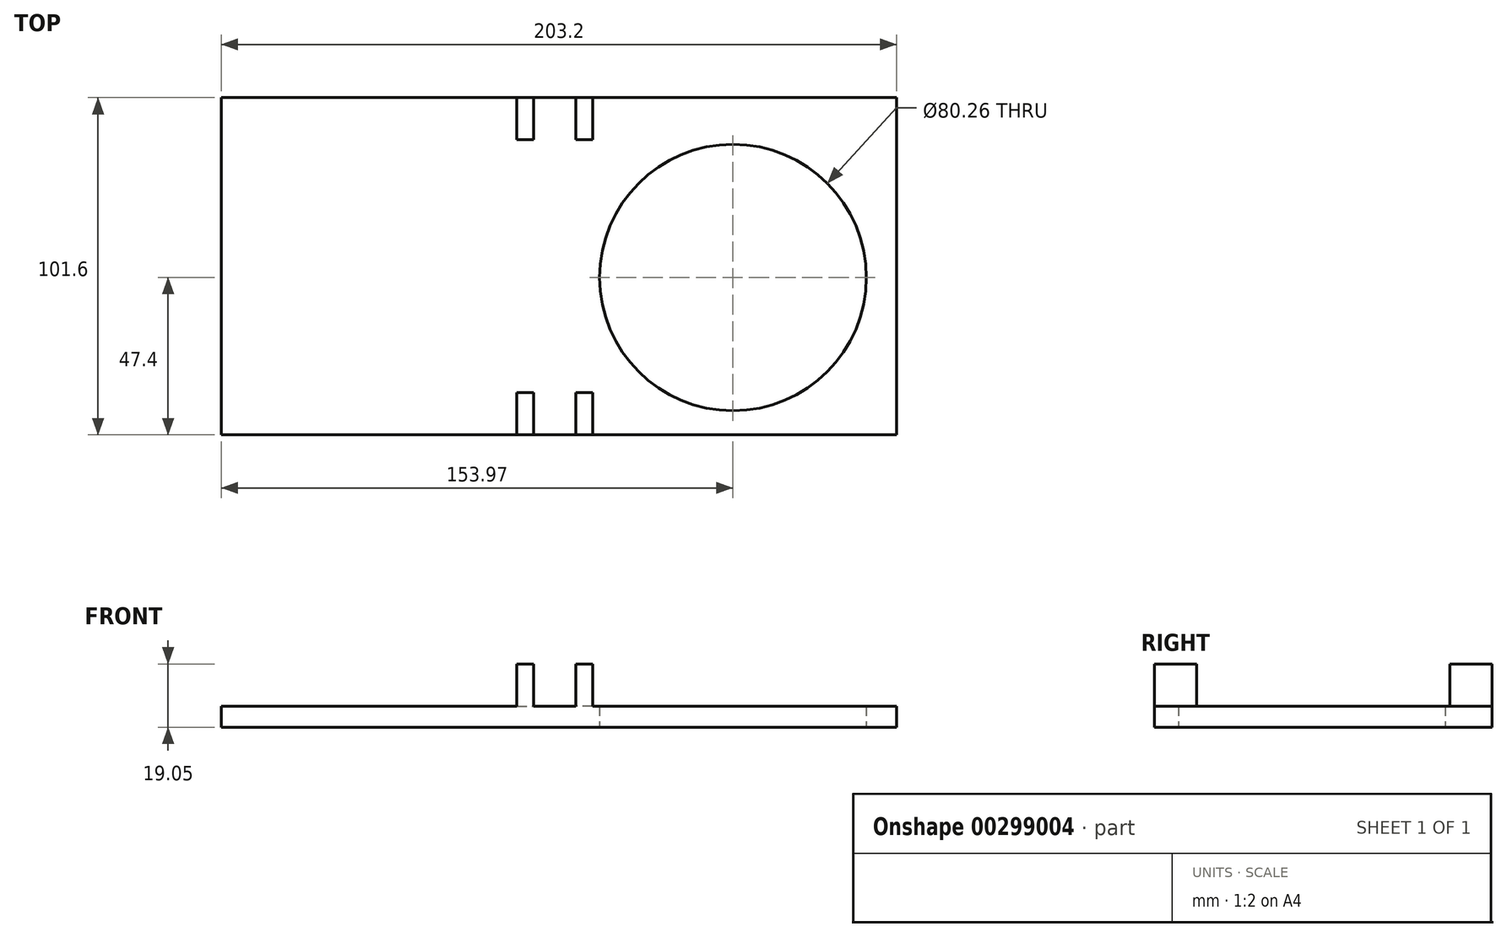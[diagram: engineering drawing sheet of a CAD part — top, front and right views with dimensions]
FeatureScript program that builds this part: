
annotation { "Feature Type Name" : "Feature", "Feature Type Description" : "" }
export const myFeature = defineFeature(function(context is Context, id is Id, definition is map)
    precondition{}
    {
        {
            var Q0;
            Q0=qCreatedBy(makeId("Top.planeOp"),FACE);
            var sketch = newSketch(context, id + "F0", { "sketchPlane" : qUnion([Q0])});
            skLineSegment(sketch, "E0.bottom", {"start": v(-77.88, 18.2) * mm, "end": v(125.32, 18.2) * mm});
            skLineSegment(sketch, "E0.top", {"start": v(-77.88, -83.4) * mm, "end": v(125.32, -83.4) * mm});
            skLineSegment(sketch, "E0.left", {"start": v(-77.88, 18.2) * mm, "end": v(-77.88, -83.4) * mm});
            skLineSegment(sketch, "E0.right", {"start": v(125.32, 18.2) * mm, "end": v(125.32, -83.4) * mm});
            skCircle(sketch, "E1", {"center": v(76.1, -36) * mm, "radius": 40.13 * mm});
            skSolve(sketch);
        }
        {
            var Q0;
            Q0 = qSketchRegion(id + "F0", true);
            extrude(context, id + "F1", {"entities" : qUnion([Q0]), "depth" : 6.35 * mm});
        }
        {
            var Q0;
            Q0=makeQuery(id+"F1.opExtrude","CAP_FACE",FACE,{"disambiguationData":[OSD([sQuery(id+"F0.wireOp",EDGE,"E0.bottom"),sQuery(id+"F0.wireOp",EDGE,"E0.top"),sQuery(id+"F0.wireOp",EDGE,"E0.left"),sQuery(id+"F0.wireOp",EDGE,"E0.right"),sQuery(id+"F0.wireOp",EDGE,"E1")])],"isStart":false});
            var sketch = newSketch(context, id + "F2", { "sketchPlane" : qUnion([Q0])});
            skLineSegment(sketch, "E2.bottom", {"start": v(33.88, -83.4) * mm, "end": v(28.8, -83.4) * mm});
            skLineSegment(sketch, "E2.top", {"start": v(33.88, -70.7) * mm, "end": v(28.8, -70.7) * mm});
            skLineSegment(sketch, "E2.left", {"start": v(33.88, -83.4) * mm, "end": v(33.88, -70.7) * mm});
            skLineSegment(sketch, "E2.right", {"start": v(28.8, -83.4) * mm, "end": v(28.8, -70.7) * mm});
            skLineSegment(sketch, "E3.bottom", {"start": v(11.02, -83.4) * mm, "end": v(16.1, -83.4) * mm});
            skLineSegment(sketch, "E3.top", {"start": v(11.02, -70.7) * mm, "end": v(16.1, -70.7) * mm});
            skLineSegment(sketch, "E3.left", {"start": v(11.02, -83.4) * mm, "end": v(11.02, -70.7) * mm});
            skLineSegment(sketch, "E3.right", {"start": v(16.1, -83.4) * mm, "end": v(16.1, -70.7) * mm});
            skLineSegment(sketch, "E4.bottom", {"start": v(33.88, 18.2) * mm, "end": v(28.8, 18.2) * mm});
            skLineSegment(sketch, "E4.top", {"start": v(33.88, 5.5) * mm, "end": v(28.8, 5.5) * mm});
            skLineSegment(sketch, "E4.left", {"start": v(33.88, 18.2) * mm, "end": v(33.88, 5.5) * mm});
            skLineSegment(sketch, "E4.right", {"start": v(28.8, 18.2) * mm, "end": v(28.8, 5.5) * mm});
            skLineSegment(sketch, "E5.bottom", {"start": v(11.02, 18.2) * mm, "end": v(16.1, 18.2) * mm});
            skLineSegment(sketch, "E5.top", {"start": v(11.02, 5.5) * mm, "end": v(16.1, 5.5) * mm});
            skLineSegment(sketch, "E5.left", {"start": v(11.02, 18.2) * mm, "end": v(11.02, 5.5) * mm});
            skLineSegment(sketch, "E5.right", {"start": v(16.1, 18.2) * mm, "end": v(16.1, 5.5) * mm});
            skSolve(sketch);
        }
        {
            var Q0;
            Q0=makeQuery(id+"F2.imprint","IMPRINT",FACE,{"disambiguationData":[TD([[makeQuery(id+"F2.imprint","IMPRINT",EDGE,{"derivedFrom":sQuery(id+"F2.wireOp",EDGE,"E3.bottom")}),1.0]])]});
            var Q1;
            Q1=makeQuery(id+"F2.imprint","IMPRINT",FACE,{"disambiguationData":[TD([[makeQuery(id+"F2.imprint","IMPRINT",EDGE,{"derivedFrom":sQuery(id+"F2.wireOp",EDGE,"E2.bottom")}),1.0]])]});
            extrude(context, id + "F3", {"entities" : qUnion([Q0, Q1]), "operationType" : NewBodyOperationType.ADD, "depth" : 12.7 * mm});
        }
        {
            var Q0;
            Q0 = qSketchRegion(id + "F2", true);
            extrude(context, id + "F4", {"entities" : qUnion([Q0]), "operationType" : NewBodyOperationType.ADD, "depth" : 12.7 * mm});
        }
    });
